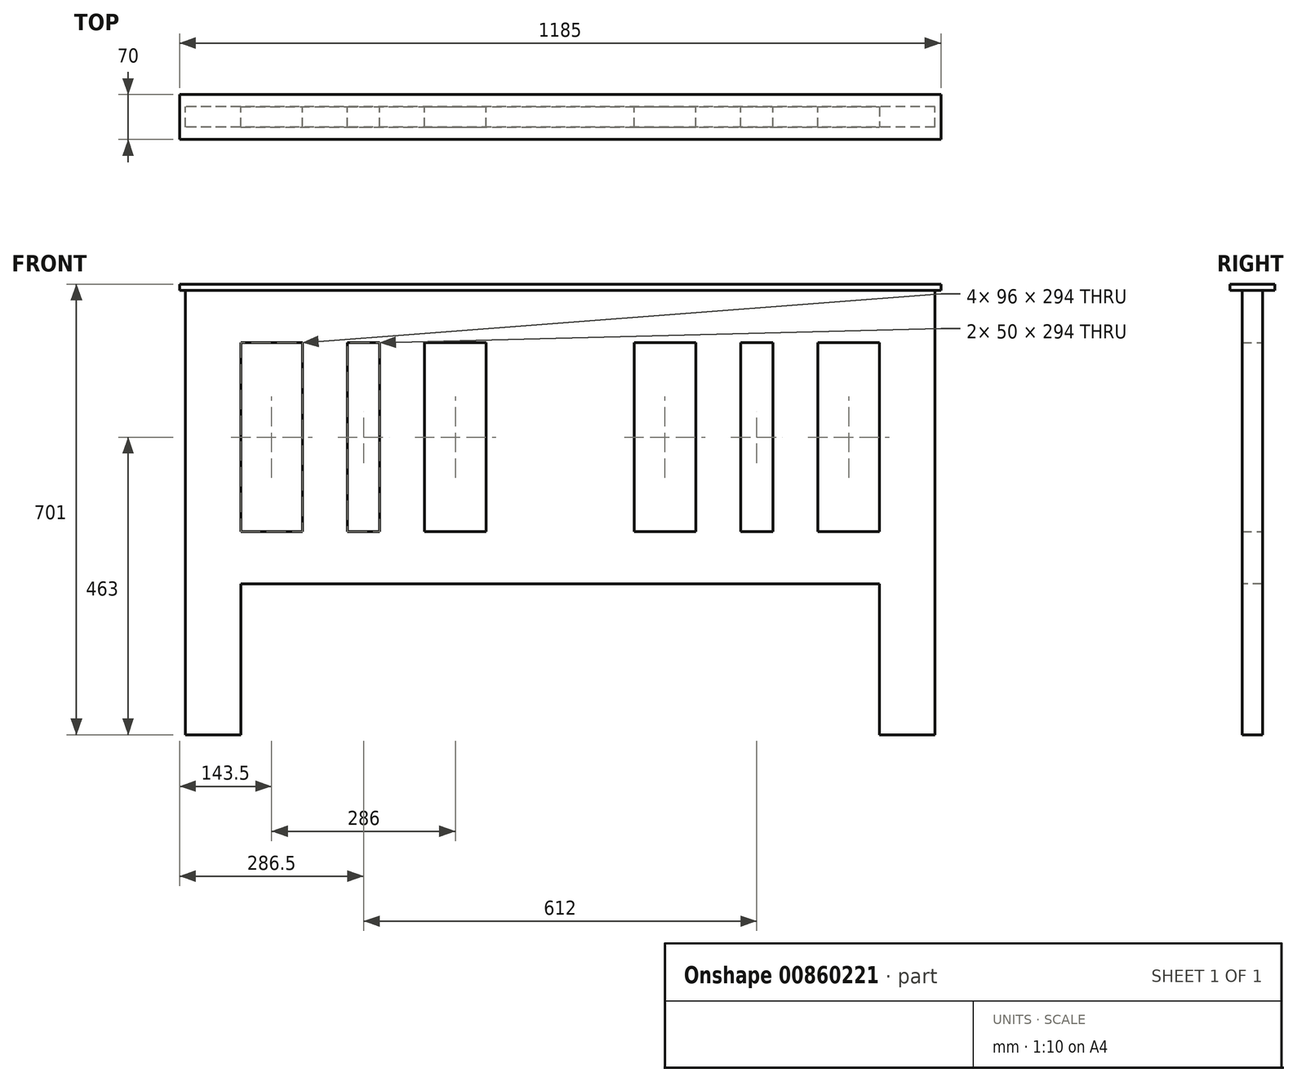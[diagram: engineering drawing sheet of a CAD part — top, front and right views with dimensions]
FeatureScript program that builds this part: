
annotation { "Feature Type Name" : "Feature", "Feature Type Description" : "" }
export const myFeature = defineFeature(function(context is Context, id is Id, definition is map)
    precondition{}
    {
        {
            var Q0;
            Q0=qCreatedBy(makeId("Top.planeOp"),FACE);
            var sketch = newSketch(context, id + "F0", { "sketchPlane" : qUnion([Q0])});
            skLineSegment(sketch, "E0.bottom", {"start": v(0, 0) * mm, "end": v(1185, 0) * mm});
            skLineSegment(sketch, "E0.top", {"start": v(0, 70) * mm, "end": v(1185, 70) * mm});
            skLineSegment(sketch, "E0.left", {"start": v(0, 0) * mm, "end": v(0, 70) * mm});
            skLineSegment(sketch, "E0.right", {"start": v(1185, 0) * mm, "end": v(1185, 70) * mm});
            skSolve(sketch);
        }
        {
            var Q0;
            Q0=makeQuery(id+"F0.imprint","IMPRINT",FACE,{"disambiguationData":[TD([[makeQuery(id+"F0.imprint","IMPRINT",EDGE,{"derivedFrom":sQuery(id+"F0.wireOp",EDGE,"E0.bottom")}),1.0]])]});
            extrude(context, id + "F1", {"entities" : qUnion([Q0]), "oppositeDirection" : true, "depth" : 10 * mm, "offsetDistance" : 25 * mm});
        }
        {
            var Q0;
            Q0=makeQuery(id+"F1.opExtrude","CAP_FACE",FACE,{"disambiguationData":[OSD([sQuery(id+"F0.wireOp",EDGE,"E0.bottom"),sQuery(id+"F0.wireOp",EDGE,"E0.top"),sQuery(id+"F0.wireOp",EDGE,"E0.left"),sQuery(id+"F0.wireOp",EDGE,"E0.right")])],"isStart":false});
            var sketch = newSketch(context, id + "F2", { "sketchPlane" : qUnion([Q0])});
            skLineSegment(sketch, "E1.bottom", {"start": v(1175.5, -19) * mm, "end": v(1089.5, -19) * mm});
            skLineSegment(sketch, "E1.top", {"start": v(1175.5, -51) * mm, "end": v(1089.5, -51) * mm});
            skLineSegment(sketch, "E1.left", {"start": v(1175.5, -19) * mm, "end": v(1175.5, -51) * mm});
            skLineSegment(sketch, "E1.right", {"start": v(1089.5, -19) * mm, "end": v(1089.5, -51) * mm});
            skLineSegment(sketch, "E2.bottom", {"start": v(95.5, -19) * mm, "end": v(9.5, -19) * mm});
            skLineSegment(sketch, "E2.top", {"start": v(95.5, -51) * mm, "end": v(9.5, -51) * mm});
            skLineSegment(sketch, "E2.left", {"start": v(95.5, -19) * mm, "end": v(95.5, -51) * mm});
            skLineSegment(sketch, "E2.right", {"start": v(9.5, -19) * mm, "end": v(9.5, -51) * mm});
            skLineSegment(sketch, "E3", {"start": v(95.5, -35) * mm, "end": v(592.5, -35) * mm, "construction": true});
            skLineSegment(sketch, "E4", {"start": v(592.5, -35) * mm, "end": v(1089.5, -35) * mm, "construction": true});
            skLineSegment(sketch, "E5", {"start": v(592.5, -35) * mm, "end": v(592.5, -70) * mm, "construction": true});
            skLineSegment(sketch, "E6", {"start": v(592.5, -35) * mm, "end": v(592.5, 0) * mm, "construction": true});
            skSolve(sketch);
        }
        {
            var Q0;
            Q0=makeQuery(id+"F2.imprint","IMPRINT",FACE,{"disambiguationData":[TD([[makeQuery(id+"F2.imprint","IMPRINT",EDGE,{"derivedFrom":sQuery(id+"F2.wireOp",EDGE,"E2.bottom")}),1.0]])]});
            var Q1;
            Q1=makeQuery(id+"F2.imprint","IMPRINT",FACE,{"disambiguationData":[TD([[makeQuery(id+"F2.imprint","IMPRINT",EDGE,{"derivedFrom":sQuery(id+"F2.wireOp",EDGE,"E1.bottom")}),1.0]])]});
            extrude(context, id + "F3", {"entities" : qUnion([Q0, Q1]), "operationType" : NewBodyOperationType.ADD, "depth" : 691 * mm, "offsetDistance" : 25 * mm});
        }
        {
            var Q0;
            Q0=makeQuery(id+"F3.opExtrude","SWEPT_FACE",FACE,{"disambiguationData":[OSD([sQuery(id+"F2.wireOp",EDGE,"E1.right")])]});
            var sketch = newSketch(context, id + "F4", { "sketchPlane" : qUnion([Q0])});
            skLineSegment(sketch, "E7.bottom", {"start": v(-51, -10) * mm, "end": v(-19, -10) * mm});
            skLineSegment(sketch, "E7.top", {"start": v(-51, -91) * mm, "end": v(-19, -91) * mm});
            skLineSegment(sketch, "E7.left", {"start": v(-51, -10) * mm, "end": v(-51, -91) * mm});
            skLineSegment(sketch, "E7.right", {"start": v(-19, -10) * mm, "end": v(-19, -91) * mm});
            skLineSegment(sketch, "E8.bottom", {"start": v(-51, -385) * mm, "end": v(-19, -385) * mm});
            skLineSegment(sketch, "E8.top", {"start": v(-51, -466) * mm, "end": v(-19, -466) * mm});
            skLineSegment(sketch, "E8.left", {"start": v(-51, -385) * mm, "end": v(-51, -466) * mm});
            skLineSegment(sketch, "E8.right", {"start": v(-19, -385) * mm, "end": v(-19, -466) * mm});
            skSolve(sketch);
        }
        {
            var Q0;
            Q0=makeQuery(id+"F4.imprint","IMPRINT",FACE,{"disambiguationData":[TD([[makeQuery(id+"F4.imprint","IMPRINT",EDGE,{"derivedFrom":sQuery(id+"F4.wireOp",EDGE,"E7.bottom")}),1.0]])]});
            var Q1;
            Q1=makeQuery(id+"F4.imprint","IMPRINT",FACE,{"disambiguationData":[TD([[makeQuery(id+"F4.imprint","IMPRINT",EDGE,{"derivedFrom":sQuery(id+"F4.wireOp",EDGE,"E8.bottom")}),-1.0]])]});
            extrude(context, id + "F5", {"entities" : qUnion([Q0, Q1]), "operationType" : NewBodyOperationType.ADD, "endBound" : BoundingType.UP_TO_NEXT, "depth" : 25 * mm, "offsetDistance" : 25 * mm});
        }
        {
            var Q0;
            Q0=makeQuery(id+"F5.opExtrude","SWEPT_FACE",FACE,{"disambiguationData":[OSD([sQuery(id+"F4.wireOp",EDGE,"E8.bottom")])]});
            var sketch = newSketch(context, id + "F6", { "sketchPlane" : qUnion([Q0])});
            skLineSegment(sketch, "E9.bottom", {"start": v(707.5, 19) * mm, "end": v(477.5, 19) * mm});
            skLineSegment(sketch, "E9.top", {"start": v(707.5, 51) * mm, "end": v(477.5, 51) * mm});
            skLineSegment(sketch, "E9.left", {"start": v(707.5, 19) * mm, "end": v(707.5, 51) * mm});
            skLineSegment(sketch, "E9.right", {"start": v(477.5, 19) * mm, "end": v(477.5, 51) * mm});
            skLineSegment(sketch, "E10", {"start": v(95.5, 35) * mm, "end": v(477.5, 35) * mm, "construction": true});
            skLineSegment(sketch, "E11", {"start": v(1089.5, 35) * mm, "end": v(707.5, 35) * mm, "construction": true});
            skLineSegment(sketch, "E12.bottom", {"start": v(993.5, 19) * mm, "end": v(923.5, 19) * mm});
            skLineSegment(sketch, "E12.top", {"start": v(993.5, 51) * mm, "end": v(923.5, 51) * mm});
            skLineSegment(sketch, "E12.left", {"start": v(993.5, 19) * mm, "end": v(993.5, 51) * mm});
            skLineSegment(sketch, "E12.right", {"start": v(923.5, 19) * mm, "end": v(923.5, 51) * mm});
            skLineSegment(sketch, "E13.bottom", {"start": v(873.5, 19) * mm, "end": v(803.5, 19) * mm});
            skLineSegment(sketch, "E13.top", {"start": v(873.5, 51) * mm, "end": v(803.5, 51) * mm});
            skLineSegment(sketch, "E13.left", {"start": v(873.5, 19) * mm, "end": v(873.5, 51) * mm});
            skLineSegment(sketch, "E13.right", {"start": v(803.5, 19) * mm, "end": v(803.5, 51) * mm});
            skLineSegment(sketch, "E14.bottom", {"start": v(381.5, 19) * mm, "end": v(311.5, 19) * mm});
            skLineSegment(sketch, "E14.top", {"start": v(381.5, 51) * mm, "end": v(311.5, 51) * mm});
            skLineSegment(sketch, "E14.left", {"start": v(381.5, 19) * mm, "end": v(381.5, 51) * mm});
            skLineSegment(sketch, "E14.right", {"start": v(311.5, 19) * mm, "end": v(311.5, 51) * mm});
            skLineSegment(sketch, "E15.bottom", {"start": v(261.5, 19) * mm, "end": v(191.5, 19) * mm});
            skLineSegment(sketch, "E15.top", {"start": v(261.5, 51) * mm, "end": v(191.5, 51) * mm});
            skLineSegment(sketch, "E15.left", {"start": v(261.5, 19) * mm, "end": v(261.5, 51) * mm});
            skLineSegment(sketch, "E15.right", {"start": v(191.5, 19) * mm, "end": v(191.5, 51) * mm});
            skLineSegment(sketch, "E16.top", {"start": v(873.5, 51) * mm, "end": v(923.5, 51) * mm});
            skLineSegment(sketch, "E16.left", {"start": v(873.5, 51) * mm, "end": v(873.5, 51) * mm});
            skLineSegment(sketch, "E16.right", {"start": v(923.5, 51) * mm, "end": v(923.5, 51) * mm});
            skLineSegment(sketch, "E17", {"start": v(1089.5, 35) * mm, "end": v(993.5, 35) * mm, "construction": true});
            skLineSegment(sketch, "E18", {"start": v(803.5, 35) * mm, "end": v(707.5, 35) * mm, "construction": true});
            skLineSegment(sketch, "E19", {"start": v(477.5, 35) * mm, "end": v(381.5, 35) * mm, "construction": true});
            skLineSegment(sketch, "E20", {"start": v(191.5, 35) * mm, "end": v(95.5, 35) * mm, "construction": true});
            skSolve(sketch);
        }
        {
            var Q0;
            Q0=makeQuery(id+"F6.imprint","IMPRINT",FACE,{"disambiguationData":[TD([[makeQuery(id+"F6.imprint","IMPRINT",EDGE,{"derivedFrom":sQuery(id+"F6.wireOp",EDGE,"E12.bottom")}),1.0]])]});
            var Q1;
            Q1=makeQuery(id+"F6.imprint","IMPRINT",FACE,{"disambiguationData":[TD([[makeQuery(id+"F6.imprint","IMPRINT",EDGE,{"derivedFrom":sQuery(id+"F6.wireOp",EDGE,"E13.bottom")}),1.0]])]});
            var Q2;
            Q2=makeQuery(id+"F6.imprint","IMPRINT",FACE,{"disambiguationData":[TD([[makeQuery(id+"F6.imprint","IMPRINT",EDGE,{"derivedFrom":sQuery(id+"F6.wireOp",EDGE,"E9.bottom")}),1.0]])]});
            var Q3;
            Q3=makeQuery(id+"F6.imprint","IMPRINT",FACE,{"disambiguationData":[TD([[makeQuery(id+"F6.imprint","IMPRINT",EDGE,{"derivedFrom":sQuery(id+"F6.wireOp",EDGE,"E14.bottom")}),1.0]])]});
            var Q4;
            Q4=makeQuery(id+"F6.imprint","IMPRINT",FACE,{"disambiguationData":[TD([[makeQuery(id+"F6.imprint","IMPRINT",EDGE,{"derivedFrom":sQuery(id+"F6.wireOp",EDGE,"E15.bottom")}),1.0]])]});
            extrude(context, id + "F7", {"entities" : qUnion([Q0, Q1, Q2, Q3, Q4]), "operationType" : NewBodyOperationType.ADD, "endBound" : BoundingType.UP_TO_NEXT, "depth" : 25 * mm, "offsetDistance" : 25 * mm});
        }
    });
